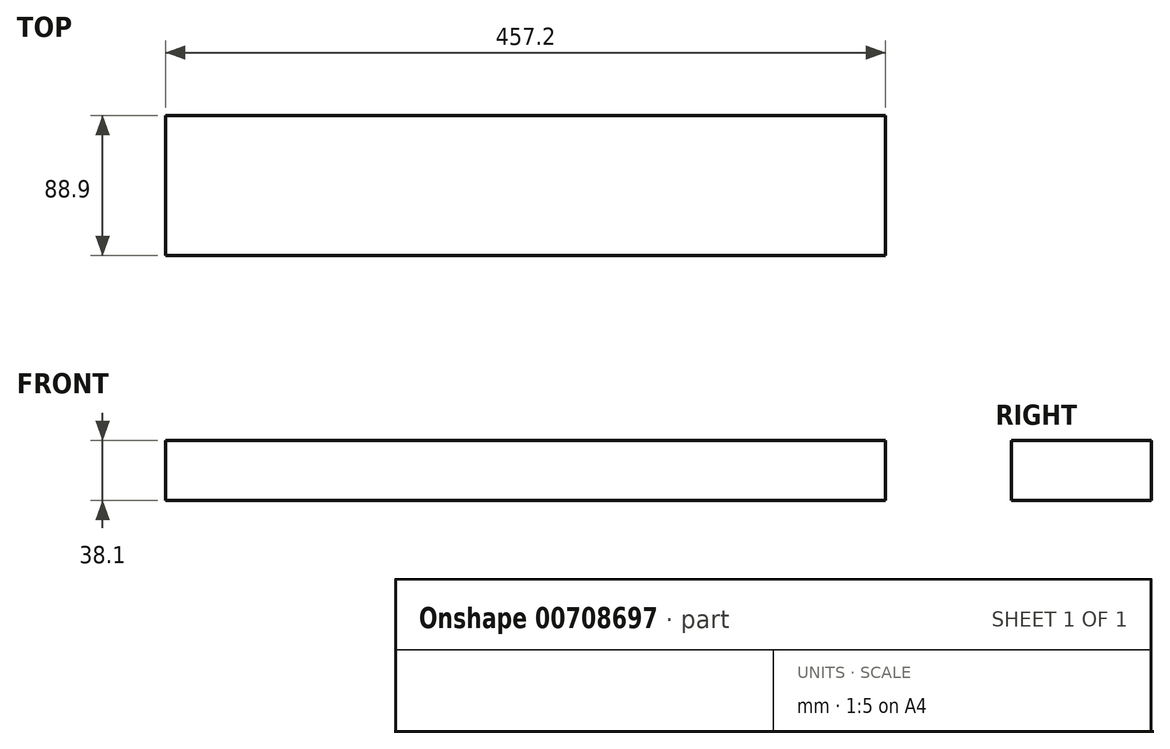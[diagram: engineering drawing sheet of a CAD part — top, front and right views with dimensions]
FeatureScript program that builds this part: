
annotation { "Feature Type Name" : "Feature", "Feature Type Description" : "" }
export const myFeature = defineFeature(function(context is Context, id is Id, definition is map)
    precondition{}
    {
        {
            var Q0;
            Q0=qCreatedBy(makeId("Right.planeOp"),FACE);
            var sketch = newSketch(context, id + "F0", { "sketchPlane" : qUnion([Q0])});
            skLineSegment(sketch, "E0.bottom", {"start": v(44.45, -19.05) * mm, "end": v(-44.45, -19.05) * mm});
            skLineSegment(sketch, "E0.top", {"start": v(44.45, 19.05) * mm, "end": v(-44.45, 19.05) * mm});
            skLineSegment(sketch, "E0.left", {"start": v(44.45, -19.05) * mm, "end": v(44.45, 19.05) * mm});
            skLineSegment(sketch, "E0.right", {"start": v(-44.45, -19.05) * mm, "end": v(-44.45, 19.05) * mm});
            skPoint(sketch, "E0.middle", {"position": v(0, 0) * mm});
            skSolve(sketch);
        }
        {
            var Q0;
            Q0=makeQuery(id+"F0.imprint","IMPRINT",FACE,{"disambiguationData":[TD([[makeQuery(id+"F0.imprint","IMPRINT",EDGE,{"derivedFrom":sQuery(id+"F0.wireOp",EDGE,"E0.bottom")}),-1.0]])]});
            extrude(context, id + "F1", {"entities" : qUnion([Q0]), "endBound" : BoundingType.SYMMETRIC, "depth" : 457.2 * mm, "offsetDistance" : 25.4 * mm});
        }
    });
